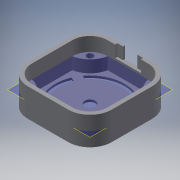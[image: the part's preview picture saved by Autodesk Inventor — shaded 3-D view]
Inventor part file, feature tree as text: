
AUTODESK INVENTOR PART (.ipt)
format: ipt  version: 2018 (Build 220112000, 112)  size: 374,272 bytes
history: native  units: mm
features: reference x21, extrude x10, sketch x9, projected_geometry x8, other x4, plane x1, pattern_circular x1
ambient origin geometry x8: Origin, YZ Plane, XZ Plane, XY Plane, X Axis, Y Axis, Z Axis, Center Point
bodies: Volumenkörper1 (feature_tree)
feature tree (54):
  other  "Querschnitt1"
  other  "Querschnitt2"
  extrude  "Extrusion1"  Depth=10.0mm
  plane  "Arbeitsebene1"
  extrude  "Extrusion2"  Depth=6.0mm
  extrude  "Extrusion3"  Depth=8.5mm TaperAngle=0.0deg
  extrude  "Extrusion4"  Depth=4.5mm
  extrude  "Extrusion5"  Depth=4.5mm
  extrude  "Extrusion6"  Depth=1.5mm TaperAngle=0.0deg
  extrude  "Extrusion7"  Depth=1.5mm TaperAngle=0.0deg
  extrude  "Extrusion8"  Depth=45.0mm
  pattern_circular  "Runde Anordnung1"  [2 undecoded]
  extrude  "Extrusion9"  Depth=1.5mm TaperAngle=0.0deg
  extrude  "Extrusion10"  Depth=1.5mm
  sketch  "Skizze1"  dims[d0=10.0mm d1=0.0mm d2=6.0mm]
  reference  "Referenz1"
  sketch  "Skizze2"  dims[d3=6.0mm d4=6.0mm]
  projected_geometry  "Projizierte Kontur1"
  reference  "Referenz2"
  reference  "Referenz3"
  sketch  "Skizze3"  dims[d5=6.0mm d6=8.5mm d7=0.0mm]
  reference  "Referenz4"
  reference  "Referenz5"
  reference  "Referenz6"
  reference  "Referenz7"
  reference  "Referenz8"
  reference  "Referenz9"
  reference  "Referenz10"
  sketch  "Skizze4"  dims[d8=4.5mm d9=4.5mm]
  projected_geometry  "Projizierte Kontur2"
  reference  "Referenz11"
  reference  "Referenz12"
  projected_geometry  "Projizierte Kontur3"
  sketch  "Skizze6"  dims[d10=4.5mm d11=4.5mm]
  reference  "Referenz13"
  sketch  "Skizze7"  dims[d12=0.15mm d13=1.5mm d14=0.0mm]
  sketch  "Skizze8"  dims[d15=1.5mm d16=0.0mm d19=8.0mm d20=0.0mm]
  reference  "Referenz14"
  reference  "Referenz15"
  reference  "Referenz16"
  reference  "Referenz17"
  reference  "Referenz18"
  reference  "Referenz19"
  reference  "Referenz20"
  reference  "Referenz21"
  projected_geometry  "Projizierte Kontur4"
  projected_geometry  "Projizierte Kontur5"
  projected_geometry  "Projizierte Kontur6"
  sketch  "Skizze9"  dims[d21=5.0mm d22=0.0mm d23=45.0mm]
  projected_geometry  "Projizierte Kontur7"
  sketch  "Skizze10"  dims[d24=1.5mm d25=1.5mm d26=5.75mm d27=0.0mm d29=3.0mm d30=3.0mm d31=2.0mm d32=0.0mm d33=30.0mm d34=360.0deg d36=10.0mm d39=0.5mm d40=2.0mm d41=-5.25mm d42=20.0mm d43=0.5mm d44=2.0mm d45=-28.25mm d46=20.0mm d47=1.7mm d48=0.0mm d49=1.5mm d50=0.0mm]
  projected_geometry  "Projizierte Kontur8"
  parser-record x1  (decoder bookkeeping rows leaked as tree rows — omitted from the tree; the rows remain in map.json)
  other  "VolumeKnob.iam"
note: 2 required parameter values undecoded (feature->parameter linkage not recoverable at this tier; creation-order binding heuristic only, values carry confidence <= 0.55)
note: 1 file-system path scrubbed to <path> (originals preserved in map.json)
